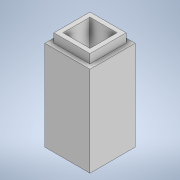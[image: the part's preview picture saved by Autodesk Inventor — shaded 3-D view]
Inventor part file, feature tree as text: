
AUTODESK INVENTOR PART (.ipt)
format: ipt  version: 2022 (Build 260153000, 153)  size: 115,200 bytes
history: native  units: in
note: dims shown in document units (in); Inventor stores cm internally (conversion verified against a paired STEP export)
features: extrude x2, sketch x2, shell x1, projected_geometry x1
ambient origin geometry x8: Origin, YZ Plane, XZ Plane, XY Plane, X Axis, Y Axis, Z Axis, Center Point
bodies: Solid1 (feature_tree)
feature tree (6):
  extrude  "Extrusion1"  Depth=0.1969in
  shell  "Shell1"  Thickness=0.3937in
  extrude  "Extrusion2"  Depth=0.0197in
  sketch  "Sketch1"  dims[d0=0.1969in d1=0.1969in d2=0.3937in d3=0.0in]
  sketch  "Sketch2"  dims[d4=0.0394in d5=0.0197in d6=0.0394in d7=0.0in]
  projected_geometry  "Projected Loop1"
